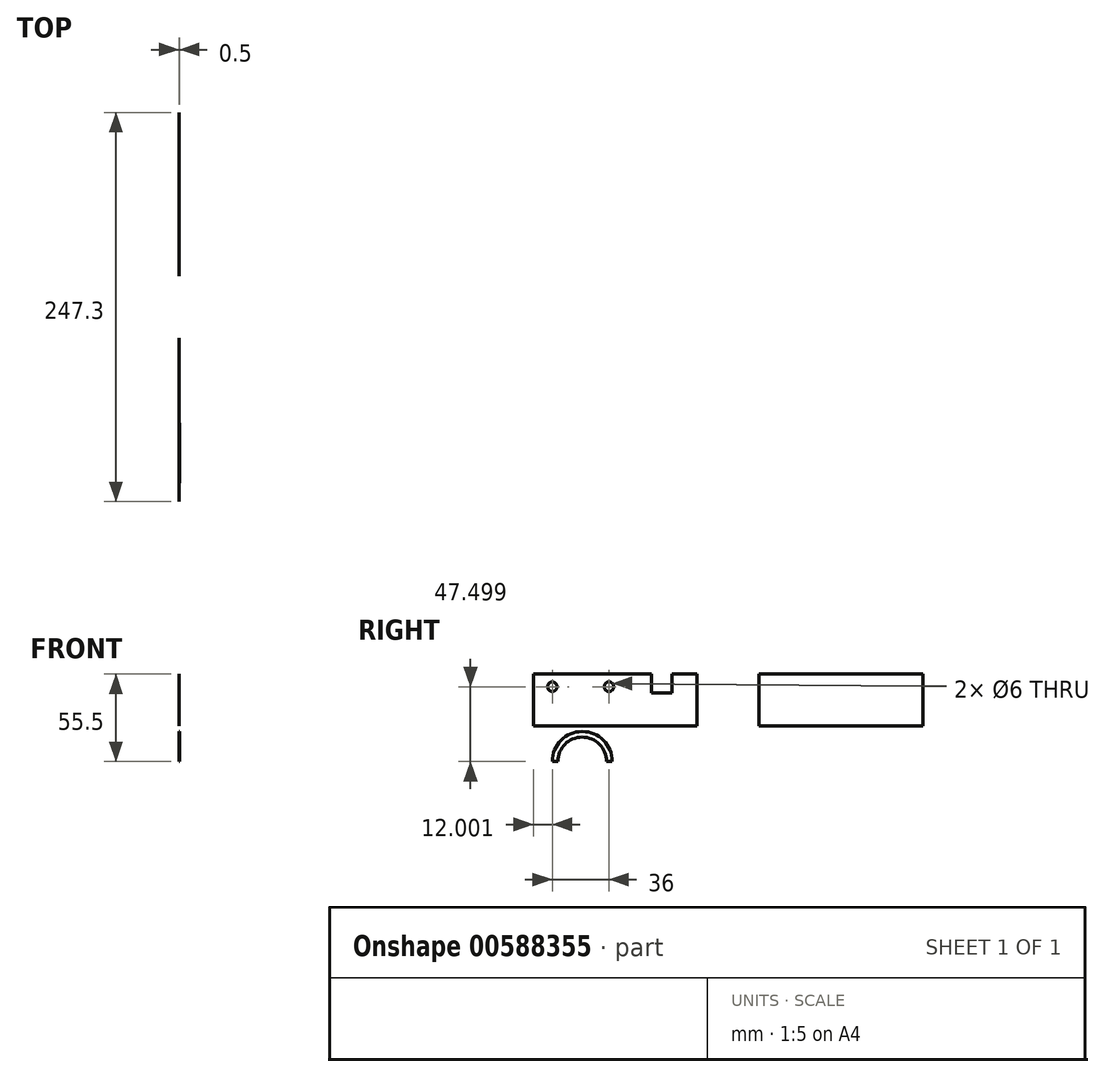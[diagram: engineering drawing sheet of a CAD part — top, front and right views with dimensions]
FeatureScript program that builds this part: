
annotation { "Feature Type Name" : "Feature", "Feature Type Description" : "" }
export const myFeature = defineFeature(function(context is Context, id is Id, definition is map)
    precondition{}
    {
        {
            var Q0;
            Q0=qCreatedBy(makeId("Right.planeOp"),FACE);
            var sketch = newSketch(context, id + "F0", { "sketchPlane" : qUnion([Q0])});
            skLineSegment(sketch, "E0.bottom", {"start": v(-22, 20.05) * mm, "end": v(-61.3, 20.05) * mm});
            skLineSegment(sketch, "E0.left", {"start": v(-22, 20.05) * mm, "end": v(-22, 52.8) * mm});
            skLineSegment(sketch, "E0.right", {"start": v(-61.3, 20.05) * mm, "end": v(-61.3, 52.8) * mm});
            skLineSegment(sketch, "E1", {"start": v(82, 20.05) * mm, "end": v(82, 52.8) * mm});
            skLineSegment(sketch, "E2", {"start": v(82, 52.8) * mm, "end": v(-22, 52.8) * mm});
            skLineSegment(sketch, "E3", {"start": v(-22, 20.05) * mm, "end": v(82, 20.05) * mm});
            skLineSegment(sketch, "E4", {"start": v(-61.3, 20.05) * mm, "end": v(-103.3, 20.05) * mm});
            skLineSegment(sketch, "E5", {"start": v(-165.3, 20.05) * mm, "end": v(-165.3, 52.8) * mm});
            skLineSegment(sketch, "E6", {"start": v(-165.3, 52.8) * mm, "end": v(-61.3, 52.8) * mm});
            skLineSegment(sketch, "E7", {"start": v(-61.3, 52.8) * mm, "end": v(-78.3, 52.8) * mm});
            skLineSegment(sketch, "E8", {"start": v(-78.3, 52.8) * mm, "end": v(-78.3, 41.8) * mm});
            skLineSegment(sketch, "E9", {"start": v(-78.3, 41.8) * mm, "end": v(-89.3, 41.8) * mm});
            skLineSegment(sketch, "E10", {"start": v(-89.3, 41.8) * mm, "end": v(-89.3, 52.8) * mm});
            skLineSegment(sketch, "E11", {"start": v(-103.3, 52.8) * mm, "end": v(-103.3, 20.05) * mm});
            skLineSegment(sketch, "E12", {"start": v(-165.3, 20.05) * mm, "end": v(-165.3, -2.7) * mm});
            skLineSegment(sketch, "E13", {"start": v(-165.3, -2.7) * mm, "end": v(-149.8, -2.7) * mm});
            skLineSegment(sketch, "E14", {"start": v(-103.3, -2.7) * mm, "end": v(-103.3, 20.05) * mm});
            skLineSegment(sketch, "E15", {"start": v(-165.3, -2.7) * mm, "end": v(-134.3, -2.7) * mm});
            skArc(sketch, "E16", {"start": v(-115.3, -2.7) * mm, "mid": v(-134.3, 16.3) * mm, "end": v(-153.3, -2.7) * mm});
            skCircle(sketch, "E17", {"center": v(-153.3, 44.8) * mm, "radius": 3 * mm});
            skCircle(sketch, "E18", {"center": v(-117.3, 44.8) * mm, "radius": 3 * mm});
            skLineSegment(sketch, "E19", {"start": v(-89.3, 52.8) * mm, "end": v(-90.3, 52.8) * mm});
            skLineSegment(sketch, "E20", {"start": v(-90.3, 52.8) * mm, "end": v(-90.3, 40.8) * mm});
            skLineSegment(sketch, "E21", {"start": v(-90.3, 40.8) * mm, "end": v(-77.3, 40.8) * mm});
            skLineSegment(sketch, "E22", {"start": v(-77.3, 40.8) * mm, "end": v(-77.3, 52.8) * mm});
            skArc(sketch, "E23", {"start": v(-118.8, -2.7) * mm, "mid": v(-134.3, 12.8) * mm, "end": v(-149.8, -2.7) * mm});
            skLineSegment(sketch, "E24.trimOffspring", {"start": v(-134.3, -2.7) * mm, "end": v(-103.3, -2.7) * mm});
            skPoint(sketch, "E25.start.orphan", {"position": v(-134.3, 16.3) * mm});
            skLineSegment(sketch, "E26", {"start": v(-165.3, 20.05) * mm, "end": v(-103.3, 20.05) * mm});
            skSolve(sketch);
        }
        {
            var Q0;
            {var subQ4=sQuery(id+"F0.wireOp",EDGE,"E0.right");Q0=makeQuery(id+"F0.imprint","IMPRINT",FACE,{"disambiguationData":[TD([[makeQuery(id+"F0.imprint","IMPRINT",EDGE,{"derivedFrom":subQ4}),1.0]])]});}
            var Q1;
            {var subQ1=sQuery(id+"F0.wireOp",EDGE,"E5");Q1=makeQuery(id+"F0.imprint","IMPRINT",FACE,{"disambiguationData":[TD([[makeQuery(id+"F0.imprint","IMPRINT",EDGE,{"derivedFrom":subQ1}),-1.0]])]});}
            var Q2;
            {var subQ0=sQuery(id+"F0.wireOp",EDGE,"536ff564-0739-4a53-a44f-9a5b6f7958c1");Q2=makeQuery(id+"F0.imprint","IMPRINT",FACE,{"disambiguationData":[TD([[makeQuery(id+"F0.imprint","IMPRINT",EDGE,{"derivedFrom":subQ0}),-1.0]])]});}
            var Q3;
            Q3=makeQuery(id+"F0.imprint","IMPRINT",FACE,{"disambiguationData":[TD([[makeQuery(id+"F0.imprint","IMPRINT",EDGE,{"derivedFrom":sQuery(id+"F0.wireOp",EDGE,"E0.left")}),-1.0]])]});
            extrude(context, id + "F1", {"entities" : qUnion([Q0, Q1, Q2, Q3]), "depth" : .3 * mm, "offsetDistance" : 25 * mm});
        }
        {
            var Q0;
            {var subQ0=sQuery(id+"F0.wireOp",EDGE,"E16");Q0=makeQuery(id+"F0.imprint","IMPRINT",FACE,{"disambiguationData":[TD([[makeQuery(id+"F0.imprint","IMPRINT",EDGE,{"derivedFrom":subQ0}),1.0]])]});}
            extrude(context, id + "F2", {"entities" : qUnion([Q0]), "operationType" : NewBodyOperationType.ADD, "depth" : .5 * mm, "offsetDistance" : 25 * mm});
        }
    });
